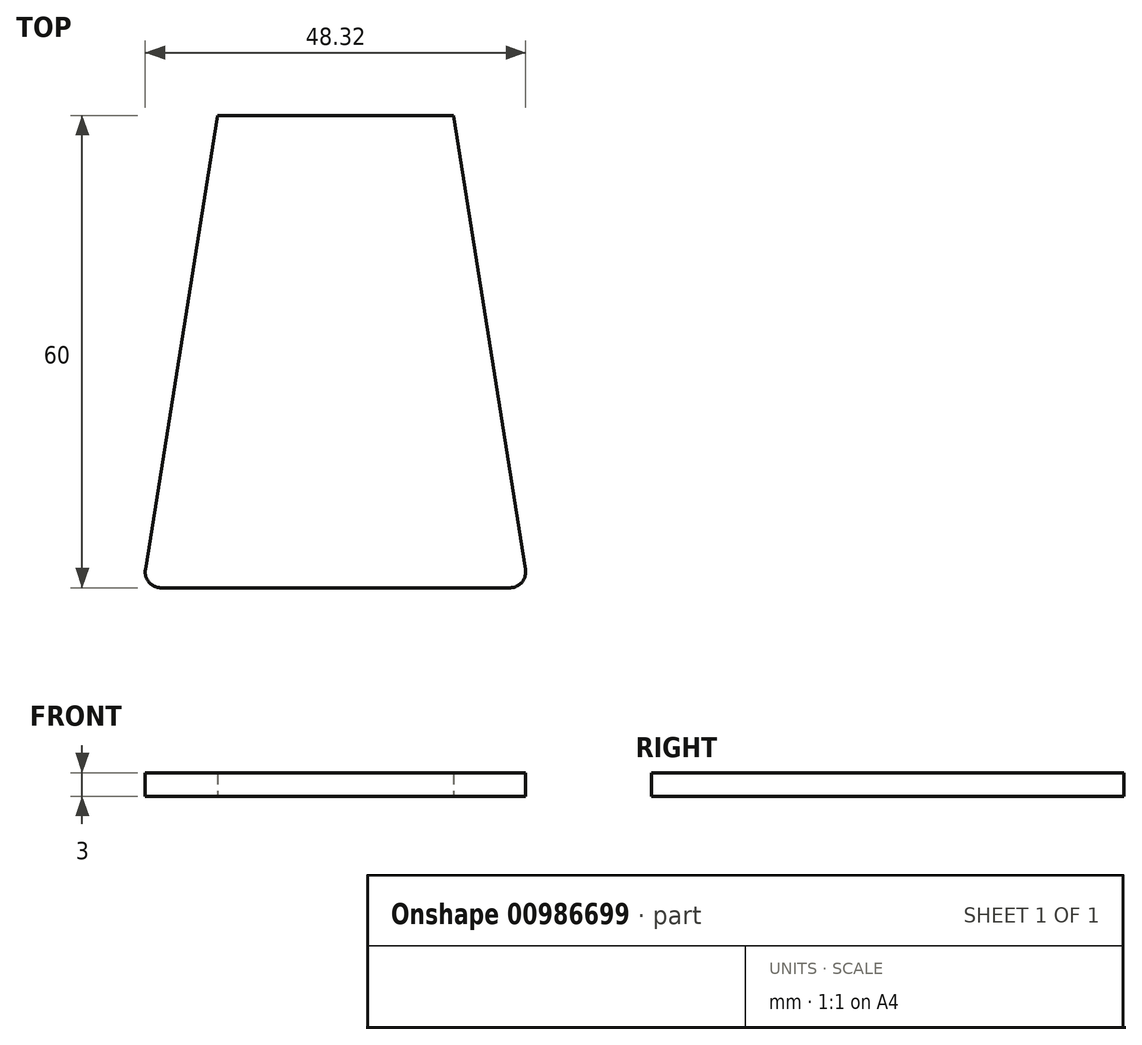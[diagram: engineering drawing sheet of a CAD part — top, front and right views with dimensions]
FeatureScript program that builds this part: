
annotation { "Feature Type Name" : "Feature", "Feature Type Description" : "" }
export const myFeature = defineFeature(function(context is Context, id is Id, definition is map)
    precondition{}
    {
        {
            var Q0;
            Q0=qCreatedBy(makeId("Top.planeOp"),FACE);
            var sketch = newSketch(context, id + "F0", { "sketchPlane" : qUnion([Q0])});
            skLineSegment(sketch, "E0", {"start": v(0, 0) * mm, "end": v(0, -60) * mm, "construction": true});
            skLineSegment(sketch, "E1", {"start": v(0, 0) * mm, "end": v(-15, 0) * mm});
            skLineSegment(sketch, "E2", {"start": v(-15, 0) * mm, "end": v(-24.14, -57.69) * mm});
            skLineSegment(sketch, "E3", {"start": v(0, -60) * mm, "end": v(-22.16, -60) * mm});
            skLineSegment(sketch, "E4.MirrorCS", {"start": v(0, 0) * mm, "end": v(15, 0) * mm});
            skLineSegment(sketch, "E5.MirrorCS", {"start": v(15, 0) * mm, "end": v(24.14, -57.69) * mm});
            skLineSegment(sketch, "E6.MirrorCS", {"start": v(0, -60) * mm, "end": v(22.16, -60) * mm});
            skPoint(sketch, "E7.visualSharp", {"position": v(-24.5, -60) * mm});
            skArc(sketch, "E7.filletArc", {"start": v(-24.14, -57.69) * mm, "mid": v(-23.68, -59.3) * mm, "end": v(-22.16, -60) * mm});
            skPoint(sketch, "E8.visualSharp", {"position": v(24.5, -60) * mm});
            skArc(sketch, "E8.filletArc", {"start": v(22.16, -60) * mm, "mid": v(23.68, -59.3) * mm, "end": v(24.14, -57.69) * mm});
            skSolve(sketch);
        }
        {
            var Q0;
            Q0=makeQuery(id+"F0.imprint","IMPRINT",FACE,{"disambiguationData":[TD([[makeQuery(id+"F0.imprint","IMPRINT",EDGE,{"derivedFrom":sQuery(id+"F0.wireOp",EDGE,"E1")}),1.0]])]});
            extrude(context, id + "F1", {"entities" : qUnion([Q0]), "depth" : 3 * mm, "offsetDistance" : 25 * mm});
        }
    });
